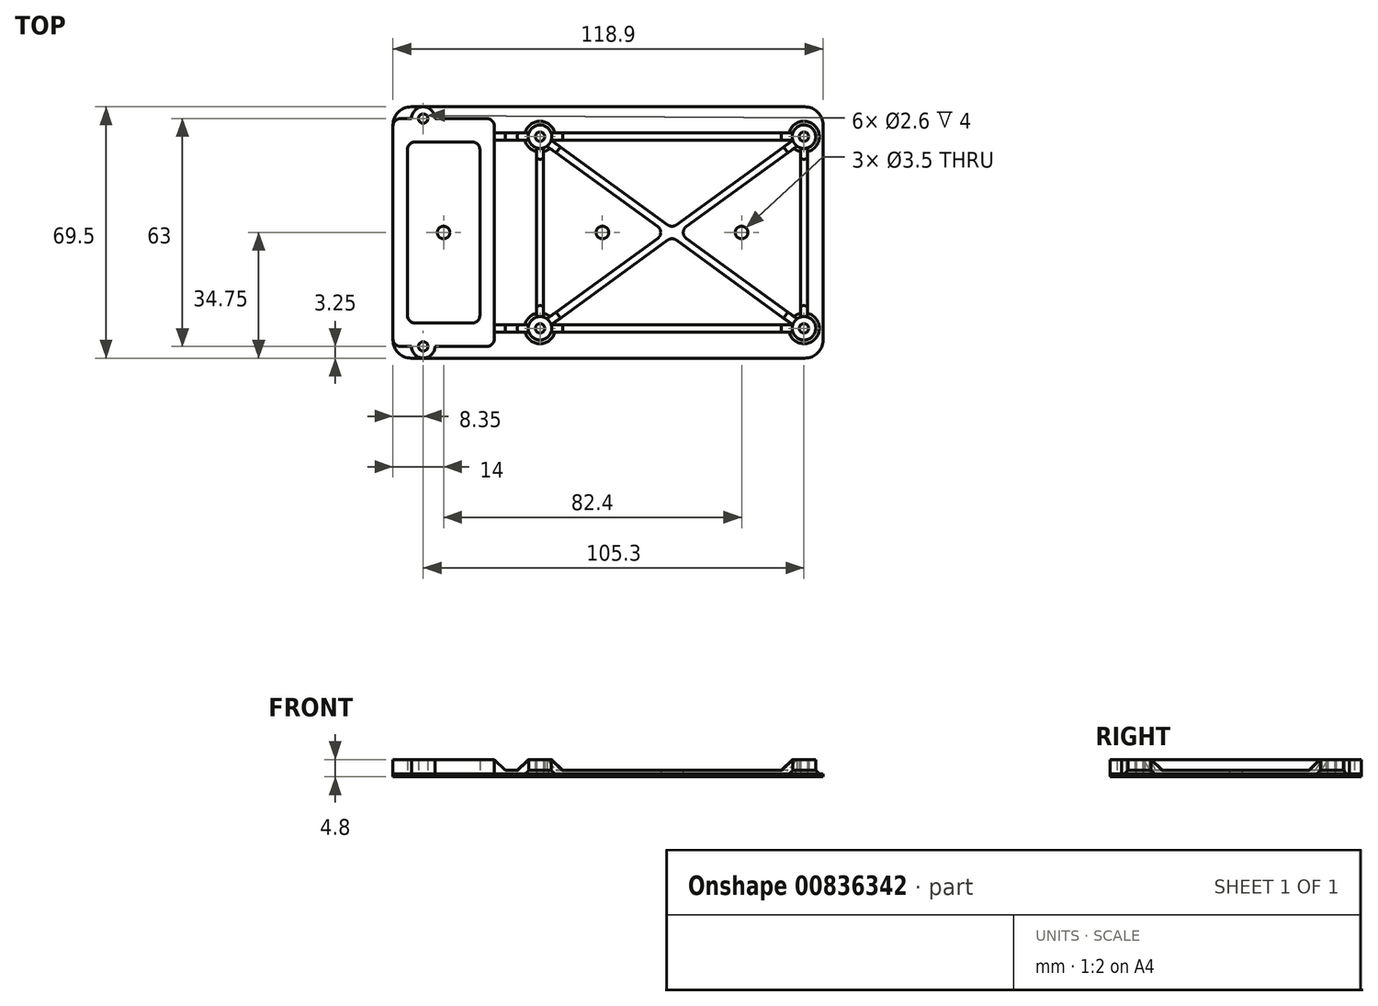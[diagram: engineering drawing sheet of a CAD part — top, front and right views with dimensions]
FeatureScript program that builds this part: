
annotation { "Feature Type Name" : "Feature", "Feature Type Description" : "" }
export const myFeature = defineFeature(function(context is Context, id is Id, definition is map)
    precondition{}
    {
        {
            assignVariable(context, id + "F0", {"name" : "topHoogte", "anyValue" : 4});
        }
        {
            var Q0;
            Q0=qCreatedBy(makeId("Top.planeOp"),FACE);
            var sketch = newSketch(context, id + "F1", { "sketchPlane" : qUnion([Q0])});
            skLineSegment(sketch, "E0.bottom", {"start": v(-19.65, 35) * mm, "end": v(19.65, 35) * mm, "construction": true});
            skLineSegment(sketch, "E0.top", {"start": v(-19.65, -35) * mm, "end": v(19.65, -35) * mm, "construction": true});
            skLineSegment(sketch, "E0.left", {"start": v(-19.65, 35) * mm, "end": v(-19.65, -35) * mm, "construction": true});
            skLineSegment(sketch, "E0.right", {"start": v(19.65, 35) * mm, "end": v(19.65, -35) * mm, "construction": true});
            skPoint(sketch, "E0.middle", {"position": v(0, 0) * mm});
            skLineSegment(sketch, "E1.bottom", {"start": v(118.65, -30) * mm, "end": v(24.65, -30) * mm, "construction": true});
            skLineSegment(sketch, "E1.top", {"start": v(118.65, 30) * mm, "end": v(24.65, 30) * mm, "construction": true});
            skLineSegment(sketch, "E1.left", {"start": v(118.65, -30) * mm, "end": v(118.65, 30) * mm, "construction": true});
            skLineSegment(sketch, "E1.right", {"start": v(24.65, -30) * mm, "end": v(24.65, 30) * mm, "construction": true});
            skPoint(sketch, "E1.middle", {"position": v(71.65, 0) * mm});
            skLineSegment(sketch, "E2", {"start": v(-5.65, 35) * mm, "end": v(-5.65, -35) * mm, "construction": true});
            skPoint(sketch, "E3", {"position": v(-5.65, 31.5) * mm});
            skPoint(sketch, "E4", {"position": v(-5.65, -31.5) * mm});
            skLineSegment(sketch, "E5", {"start": v(24.65, 26.5) * mm, "end": v(118.65, 26.5) * mm, "construction": true});
            skLineSegment(sketch, "E6", {"start": v(24.65, -26.5) * mm, "end": v(118.65, -26.5) * mm, "construction": true});
            skPoint(sketch, "E7", {"position": v(26.65, 26.5) * mm});
            skPoint(sketch, "E8", {"position": v(26.65, -26.5) * mm});
            skPoint(sketch, "E9", {"position": v(99.65, 26.5) * mm});
            skPoint(sketch, "E10", {"position": v(99.65, -26.5) * mm});
            skLineSegment(sketch, "E11", {"start": v(26.65, -26.5) * mm, "end": v(99.65, 26.5) * mm, "construction": true});
            skPoint(sketch, "E12", {"position": v(63.15, 0) * mm});
            skPoint(sketch, "E13", {"position": v(43.9, 0) * mm});
            skLineSegment(sketch, "E14", {"start": v(63.15, 0) * mm, "end": v(63.15, 13.4) * mm, "construction": true});
            skLineSegment(sketch, "E15", {"start": v(63.15, 0) * mm, "end": v(24.65, 0) * mm, "construction": true});
            skPoint(sketch, "E16.MirrorP", {"position": v(82.4, 0) * mm});
            skSolve(sketch);
        }
        {
            var Q0;
            Q0=qCreatedBy(makeId("Top.planeOp"),FACE);
            var sketch = newSketch(context, id + "F2", { "sketchPlane" : qUnion([Q0])});
            skLineSegment(sketch, "E17.bottom", {"start": v(-12, 31.5) * mm, "end": v(12, 31.5) * mm});
            skLineSegment(sketch, "E17.top", {"start": v(-12, -31.5) * mm, "end": v(12, -31.5) * mm});
            skLineSegment(sketch, "E17.left", {"start": v(-14, 29.5) * mm, "end": v(-14, -29.5) * mm});
            skLineSegment(sketch, "E17.right", {"start": v(14, 29.5) * mm, "end": v(14, -29.5) * mm});
            skPoint(sketch, "E17.middle", {"position": v(0, 0) * mm});
            skLineSegment(sketch, "E18.bottom", {"start": v(8, -25) * mm, "end": v(-8, -25) * mm});
            skLineSegment(sketch, "E18.top", {"start": v(8, 25) * mm, "end": v(-8, 25) * mm});
            skLineSegment(sketch, "E18.left", {"start": v(10, -23) * mm, "end": v(10, 23) * mm});
            skLineSegment(sketch, "E18.right", {"start": v(-10, -23) * mm, "end": v(-10, 23) * mm});
            skPoint(sketch, "E19.visualSharp", {"position": v(-10, 25) * mm});
            skArc(sketch, "E19.filletArc", {"start": v(-8, 25) * mm, "mid": v(-9.41, 24.41) * mm, "end": v(-10, 23) * mm});
            skPoint(sketch, "E20.visualSharp", {"position": v(10, 25) * mm});
            skArc(sketch, "E20.filletArc", {"start": v(10, 23) * mm, "mid": v(9.41, 24.41) * mm, "end": v(8, 25) * mm});
            skPoint(sketch, "E21.visualSharp", {"position": v(10, -25) * mm});
            skArc(sketch, "E21.filletArc", {"start": v(8, -25) * mm, "mid": v(9.41, -24.41) * mm, "end": v(10, -23) * mm});
            skPoint(sketch, "E22.visualSharp", {"position": v(-10, -25) * mm});
            skArc(sketch, "E22.filletArc", {"start": v(-10, -23) * mm, "mid": v(-9.41, -24.41) * mm, "end": v(-8, -25) * mm});
            skPoint(sketch, "E23.visualSharp", {"position": v(-14, -31.5) * mm});
            skArc(sketch, "E23.filletArc", {"start": v(-14, -29.5) * mm, "mid": v(-13.41, -30.91) * mm, "end": v(-12, -31.5) * mm});
            skPoint(sketch, "E24.visualSharp", {"position": v(14, -31.5) * mm});
            skArc(sketch, "E24.filletArc", {"start": v(12, -31.5) * mm, "mid": v(13.41, -30.91) * mm, "end": v(14, -29.5) * mm});
            skPoint(sketch, "E25.visualSharp", {"position": v(14, 31.5) * mm});
            skArc(sketch, "E25.filletArc", {"start": v(14, 29.5) * mm, "mid": v(13.41, 30.91) * mm, "end": v(12, 31.5) * mm});
            skPoint(sketch, "E26.visualSharp", {"position": v(-14, 31.5) * mm});
            skArc(sketch, "E26.filletArc", {"start": v(-12, 31.5) * mm, "mid": v(-13.41, 30.91) * mm, "end": v(-14, 29.5) * mm});
            skSolve(sketch);
        }
        {
            var Q0;
            Q0 = qSketchRegion(id + "F2", true);
            extrude(context, id + "F3", {"entities" : qUnion([Q0]), "depth" : (getVariable(context, 'topHoogte')) * mm, "offsetDistance" : 25 * mm});
        }
        {
            var Q0;
            Q0=qCreatedBy(makeId("Top.planeOp"),FACE);
            var sketch = newSketch(context, id + "F4", { "sketchPlane" : qUnion([Q0])});
            skPoint(sketch, "E27", {"position": v(99.65, 26.5) * mm});
            skPoint(sketch, "E28", {"position": v(99.65, -26.5) * mm});
            skLineSegment(sketch, "E29.0", {"start": v(14, 29.5) * mm, "end": v(14, -29.5) * mm, "construction": true});
            skLineSegment(sketch, "E30", {"start": v(99.65, -26.5) * mm, "end": v(14, -26.5) * mm, "construction": true});
            skLineSegment(sketch, "E31", {"start": v(99.65, 26.5) * mm, "end": v(14, 26.5) * mm, "construction": true});
            skLineSegment(sketch, "E32", {"start": v(99.65, 26.5) * mm, "end": v(99.65, -26.5) * mm, "construction": true});
            skArc(sketch, "E33.0.startCap", {"start": v(99.65, 27.5) * mm, "mid": v(100.36, 27.2) * mm, "end": v(100.65, 26.5) * mm});
            skArc(sketch, "E33.0.endCap", {"start": v(14, 25.5) * mm, "mid": v(13, 26.5) * mm, "end": v(14, 27.5) * mm});
            skLineSegment(sketch, "E33.0.right", {"start": v(99.65, 27.5) * mm, "end": v(14, 27.5) * mm});
            skArc(sketch, "E33.1.startCap", {"start": v(99.65, 27.5) * mm, "mid": v(100.36, 27.2) * mm, "end": v(100.65, 26.5) * mm});
            skArc(sketch, "E33.1.endCap", {"start": v(100.65, -26.5) * mm, "mid": v(100.36, -27.2) * mm, "end": v(99.65, -27.5) * mm});
            skLineSegment(sketch, "E33.1.left", {"start": v(100.65, 26.5) * mm, "end": v(100.65, -26.5) * mm});
            skLineSegment(sketch, "E33.1.right", {"start": v(98.65, 24.54) * mm, "end": v(98.65, -24.54) * mm});
            skArc(sketch, "E33.2.startCap", {"start": v(100.65, -26.5) * mm, "mid": v(100.36, -27.2) * mm, "end": v(99.65, -27.5) * mm});
            skArc(sketch, "E33.2.endCap", {"start": v(14, -27.5) * mm, "mid": v(13, -26.5) * mm, "end": v(14, -25.5) * mm});
            skLineSegment(sketch, "E33.2.left", {"start": v(99.65, -27.5) * mm, "end": v(14, -27.5) * mm});
            skPoint(sketch, "E34", {"position": v(26.65, 26.5) * mm});
            skPoint(sketch, "E35", {"position": v(26.65, -26.5) * mm});
            skLineSegment(sketch, "E36", {"start": v(26.65, -26.5) * mm, "end": v(26.65, 26.5) * mm, "construction": true});
            skLineSegment(sketch, "E37", {"start": v(25.65, 25.5) * mm, "end": v(25.65, -25.5) * mm});
            skLineSegment(sketch, "E38", {"start": v(27.65, -24.54) * mm, "end": v(27.65, 24.54) * mm});
            skLineSegment(sketch, "E39.trimOffspring", {"start": v(25.65, -25.5) * mm, "end": v(14, -25.5) * mm});
            skLineSegment(sketch, "E40.trimOffspring", {"start": v(25.65, 25.5) * mm, "end": v(14, 25.5) * mm});
            skLineSegment(sketch, "E41", {"start": v(26.65, 26.5) * mm, "end": v(99.65, -26.5) * mm, "construction": true});
            skLineSegment(sketch, "E42", {"start": v(99.65, 26.5) * mm, "end": v(26.65, -26.5) * mm, "construction": true});
            skLineSegment(sketch, "E43", {"start": v(29.73, 25.5) * mm, "end": v(61.97, 2.09) * mm});
            skLineSegment(sketch, "E44", {"start": v(96.57, -25.5) * mm, "end": v(64.33, -2.09) * mm});
            skLineSegment(sketch, "E45.trimOffspring", {"start": v(96.57, -25.5) * mm, "end": v(29.73, -25.5) * mm});
            skLineSegment(sketch, "E46", {"start": v(27.65, -24.54) * mm, "end": v(59.22, -1.62) * mm});
            skLineSegment(sketch, "E47", {"start": v(98.65, 24.54) * mm, "end": v(67.08, 1.62) * mm});
            skLineSegment(sketch, "E48.trimOffspring", {"start": v(96.57, 25.5) * mm, "end": v(29.73, 25.5) * mm});
            skLineSegment(sketch, "E49.trimOffspring", {"start": v(67.08, -1.62) * mm, "end": v(98.65, -24.54) * mm});
            skLineSegment(sketch, "E50.trimOffspring", {"start": v(64.33, 2.09) * mm, "end": v(96.57, 25.5) * mm});
            skLineSegment(sketch, "E51.trimOffspring", {"start": v(59.22, 1.62) * mm, "end": v(27.65, 24.54) * mm});
            skLineSegment(sketch, "E52.trimOffspring", {"start": v(61.97, -2.09) * mm, "end": v(29.73, -25.5) * mm});
            skPoint(sketch, "E53.trimOffspring.end.orphan", {"position": v(27.65, -25.5) * mm});
            skPoint(sketch, "E54.visualSharp", {"position": v(63.15, -1.24) * mm});
            skArc(sketch, "E54.filletArc", {"start": v(64.33, -2.09) * mm, "mid": v(63.15, -1.7) * mm, "end": v(61.97, -2.09) * mm});
            skPoint(sketch, "E55.visualSharp", {"position": v(64.85, 0) * mm});
            skArc(sketch, "E55.filletArc", {"start": v(67.08, 1.62) * mm, "mid": v(66.26, 0) * mm, "end": v(67.08, -1.62) * mm});
            skPoint(sketch, "E56.visualSharp", {"position": v(61.45, 0) * mm});
            skArc(sketch, "E56.filletArc", {"start": v(59.22, -1.62) * mm, "mid": v(60.04, 0) * mm, "end": v(59.22, 1.62) * mm});
            skPoint(sketch, "E57.visualSharp", {"position": v(63.15, 1.24) * mm});
            skArc(sketch, "E57.filletArc", {"start": v(61.97, 2.09) * mm, "mid": v(63.15, 1.7) * mm, "end": v(64.33, 2.09) * mm});
            skSolve(sketch);
        }
        {
            var Q0;
            Q0 = qSketchRegion(id + "F4", true);
            extrude(context, id + "F5", {"entities" : qUnion([Q0]), "operationType" : NewBodyOperationType.ADD, "depth" : 1 * mm, "offsetDistance" : 25 * mm});
        }
        {
            var Q0;
            Q0=makeQuery(id+"F3.opExtrude","CAP_FACE",FACE,{"disambiguationData":[OSD([sQuery(id+"F2.wireOp",EDGE,"E17.bottom"),sQuery(id+"F2.wireOp",EDGE,"E17.top"),sQuery(id+"F2.wireOp",EDGE,"E17.left"),sQuery(id+"F2.wireOp",EDGE,"E17.right"),sQuery(id+"F2.wireOp",EDGE,"Aoumscto-ISyM-bLo6-r2er-gqb8EqtCcs1s.bottom"),sQuery(id+"F2.wireOp",EDGE,"Aoumscto-ISyM-bLo6-r2er-gqb8EqtCcs1s.top"),sQuery(id+"F2.wireOp",EDGE,"Aoumscto-ISyM-bLo6-r2er-gqb8EqtCcs1s.left"),sQuery(id+"F2.wireOp",EDGE,"Aoumscto-ISyM-bLo6-r2er-gqb8EqtCcs1s.right"),sQuery(id+"F2.wireOp",EDGE,"S9hbntlY-zaf4-CZbE-wMCd-JAsEF4PvGXqu"),sQuery(id+"F2.wireOp",EDGE,"iUlIFxYP-P7sP-15qZ-lrAx-pwGYtXNXY4pD")])],"isStart":true});
            var sketch = newSketch(context, id + "F6", { "sketchPlane" : qUnion([Q0])});
            skCircle(sketch, "E58", {"center": v(-5.65, -31.5) * mm, "radius": 3.25 * mm});
            skCircle(sketch, "E59", {"center": v(-5.65, 31.5) * mm, "radius": 3.25 * mm});
            skCircle(sketch, "E60", {"center": v(99.65, 26.5) * mm, "radius": 3.25 * mm});
            skCircle(sketch, "E61", {"center": v(99.65, -26.5) * mm, "radius": 3.25 * mm});
            skCircle(sketch, "E62", {"center": v(26.65, -26.5) * mm, "radius": 3.25 * mm});
            skCircle(sketch, "E63", {"center": v(26.65, 26.5) * mm, "radius": 3.25 * mm});
            skSolve(sketch);
        }
        {
            var Q0;
            Q0 = qSketchRegion(id + "F6", true);
            extrude(context, id + "F7", {"entities" : qUnion([Q0]), "operationType" : NewBodyOperationType.ADD, "oppositeDirection" : true, "depth" : (getVariable(context, 'topHoogte')) * mm, "offsetDistance" : 25 * mm});
        }
        {
            var Q0;
            Q0=qCreatedBy(makeId("Top.planeOp"),FACE);
            var sketch = newSketch(context, id + "F8", { "sketchPlane" : qUnion([Q0])});
            skLineSegment(sketch, "E64.0", {"start": v(-14, 29.5) * mm, "end": v(-14, -29.5) * mm, "construction": true});
            skArc(sketch, "E65.0", {"start": v(96.56, 27.5) * mm, "mid": v(101.95, 28.8) * mm, "end": v(100.65, 23.4) * mm, "construction": true});
            skLineSegment(sketch, "E66.0", {"start": v(24.65, 26.5) * mm, "end": v(118.65, 26.5) * mm, "construction": true});
            skArc(sketch, "E67.0", {"start": v(100.65, -23.4) * mm, "mid": v(101.95, -28.8) * mm, "end": v(96.56, -27.5) * mm, "construction": true});
            skLineSegment(sketch, "E68.0", {"start": v(24.65, -26.5) * mm, "end": v(118.65, -26.5) * mm, "construction": true});
            skLineSegment(sketch, "E69.bottom", {"start": v(104.9, 34.75) * mm, "end": v(-14, 34.75) * mm});
            skLineSegment(sketch, "E69.top", {"start": v(104.9, -34.75) * mm, "end": v(-14, -34.75) * mm});
            skLineSegment(sketch, "E69.left", {"start": v(102.9, 34.75) * mm, "end": v(102.9, -34.75) * mm, "construction": true});
            skLineSegment(sketch, "E69.right", {"start": v(-14, 34.75) * mm, "end": v(-14, -34.75) * mm});
            skPoint(sketch, "E70", {"position": v(102.9, 26.5) * mm});
            skPoint(sketch, "E71", {"position": v(-5.65, 34.75) * mm});
            skLineSegment(sketch, "E72", {"start": v(104.9, 34.75) * mm, "end": v(104.9, -34.75) * mm});
            skPoint(sketch, "E73.orphan", {"position": v(104.9, -34.75) * mm});
            skSolve(sketch);
        }
        {
            var Q0;
            Q0 = qSketchRegion(id + "F8", true);
            extrude(context, id + "F9", {"entities" : qUnion([Q0]), "operationType" : NewBodyOperationType.ADD, "oppositeDirection" : true, "depth" : 0.8 * mm, "offsetDistance" : 25 * mm});
        }
        {
            var Q0;
            Q0=makeQuery(id+"F9.opExtrude","SWEPT_EDGE",EDGE,{"disambiguationData":[OSD([sQuery(id+"F8.wireOp",EDGE,"E69.top"),sQuery(id+"F8.wireOp",EDGE,"E69.right")])]});
            var Q1;
            Q1=makeQuery(id+"F9.opExtrude","SWEPT_EDGE",EDGE,{"disambiguationData":[OSD([sQuery(id+"F8.wireOp",EDGE,"E69.bottom"),sQuery(id+"F8.wireOp",EDGE,"E69.right")])]});
            var Q2;
            Q2=makeQuery(id+"F9.opExtrude","SWEPT_EDGE",EDGE,{"disambiguationData":[OSD([sQuery(id+"F8.wireOp",EDGE,"E69.bottom"),sQuery(id+"F8.wireOp",EDGE,"E69.left")])]});
            var Q3;
            Q3=makeQuery(id+"F9.opExtrude","SWEPT_EDGE",EDGE,{"disambiguationData":[OSD([sQuery(id+"F8.wireOp",EDGE,"E69.top"),sQuery(id+"F8.wireOp",EDGE,"E69.left")])]});
            fillet(context, id + "F10", {"entities" : qUnion([Q0, Q1, Q2, Q3]), "radius" : 5 * mm, "tangentPropagation" : true, "allowEdgeOverflow" : false});
        }
        {
            var Q0;
            Q0=sQuery(id+"F1.wireOp",VERTEX,"E9");
            var Q1;
            Q1=sQuery(id+"F1.wireOp",VERTEX,"E7");
            var Q2;
            Q2=sQuery(id+"F1.wireOp",VERTEX,"E3");
            var Q3;
            Q3=sQuery(id+"F1.wireOp",VERTEX,"E4");
            var Q4;
            Q4=sQuery(id+"F1.wireOp",VERTEX,"E8");
            var Q5;
            Q5=sQuery(id+"F1.wireOp",VERTEX,"E10");
            var Q6;
            Q6=makeQuery(id+"F3.opExtrude","SWEPT_BODY",BODY,{"disambiguationData":[OSD([sQuery(id+"F2.wireOp",EDGE,"E17.bottom"),sQuery(id+"F2.wireOp",EDGE,"E17.top"),sQuery(id+"F2.wireOp",EDGE,"E17.left"),sQuery(id+"F2.wireOp",EDGE,"Aoumscto-ISyM-bLo6-r2er-gqb8EqtCcs1s.bottom"),sQuery(id+"F2.wireOp",EDGE,"Aoumscto-ISyM-bLo6-r2er-gqb8EqtCcs1s.top"),sQuery(id+"F2.wireOp",EDGE,"Aoumscto-ISyM-bLo6-r2er-gqb8EqtCcs1s.right"),sQuery(id+"F2.wireOp",EDGE,"sPsnzCd1-hEix-0JZU-3coD-6OnEEw0yhwWd"),sQuery(id+"F2.wireOp",EDGE,"XCQeSn6e-DVvC-qXyd-qOtz-2lCuqoaPEOlS")])]});
            hole(context, id + "F11", {"style" : HoleStyle.SIMPLE, "endStyle" : HoleEndStyle.THROUGH, "oppositeDirection" : true, "holeDiameter" : 2.6 * mm, "majorDiameter" : 5 * mm, "isTappedThrough" : true, "tappedDepth" : 12 * mm, "tapClearance" : 3, "locations" : qUnion([Q0, Q1, Q2, Q3, Q4, Q5]), "scope" : qUnion([Q6])});
        }
        {
            var Q0;
            Q0=makeQuery(id+"F7.boolean.opBoolean","INTERSECT",EDGE,{"disambiguationData":[OD(2.0)],"derivedFrom":[makeQuery(id+"F5.opExtrude","CAP_FACE",FACE,{"disambiguationData":[OSD([sQuery(id+"F4.wireOp",EDGE,"E33.0.endCap"),sQuery(id+"F4.wireOp",EDGE,"E33.0.left"),sQuery(id+"F4.wireOp",EDGE,"E33.0.right"),sQuery(id+"F4.wireOp",EDGE,"E33.1.startCap"),sQuery(id+"F4.wireOp",EDGE,"E33.1.left"),sQuery(id+"F4.wireOp",EDGE,"E33.1.right"),sQuery(id+"F4.wireOp",EDGE,"E33.2.startCap"),sQuery(id+"F4.wireOp",EDGE,"E33.2.endCap"),sQuery(id+"F4.wireOp",EDGE,"E33.2.left"),sQuery(id+"F4.wireOp",EDGE,"E33.2.right"),sQuery(id+"F4.wireOp",EDGE,"E37"),sQuery(id+"F4.wireOp",EDGE,"E38"),sQuery(id+"F4.wireOp",EDGE,"E39.trimOffspring"),sQuery(id+"F4.wireOp",EDGE,"E40.trimOffspring")])],"isStart":false}),makeQuery(id+"F7.opExtrude","SWEPT_FACE",FACE,{"disambiguationData":[OSD([sQuery(id+"F6.wireOp",EDGE,"E63")])]})]});
            var Q1;
            Q1=makeQuery(id+"F7.boolean.opBoolean","INTERSECT",EDGE,{"disambiguationData":[OD(1.0)],"derivedFrom":[makeQuery(id+"F5.opExtrude","CAP_FACE",FACE,{"disambiguationData":[OSD([sQuery(id+"F4.wireOp",EDGE,"E33.0.endCap"),sQuery(id+"F4.wireOp",EDGE,"E33.0.left"),sQuery(id+"F4.wireOp",EDGE,"E33.0.right"),sQuery(id+"F4.wireOp",EDGE,"E33.1.startCap"),sQuery(id+"F4.wireOp",EDGE,"E33.1.left"),sQuery(id+"F4.wireOp",EDGE,"E33.1.right"),sQuery(id+"F4.wireOp",EDGE,"E33.2.startCap"),sQuery(id+"F4.wireOp",EDGE,"E33.2.endCap"),sQuery(id+"F4.wireOp",EDGE,"E33.2.left"),sQuery(id+"F4.wireOp",EDGE,"E33.2.right"),sQuery(id+"F4.wireOp",EDGE,"E37"),sQuery(id+"F4.wireOp",EDGE,"E38"),sQuery(id+"F4.wireOp",EDGE,"E39.trimOffspring"),sQuery(id+"F4.wireOp",EDGE,"E40.trimOffspring")])],"isStart":false}),makeQuery(id+"F7.opExtrude","SWEPT_FACE",FACE,{"disambiguationData":[OSD([sQuery(id+"F6.wireOp",EDGE,"E63")])]})]});
            var Q2;
            Q2=makeQuery(id+"F7.boolean.opBoolean","INTERSECT",EDGE,{"disambiguationData":[OD(0.0)],"derivedFrom":[makeQuery(id+"F5.opExtrude","CAP_FACE",FACE,{"disambiguationData":[OSD([sQuery(id+"F4.wireOp",EDGE,"E33.0.endCap"),sQuery(id+"F4.wireOp",EDGE,"E33.0.left"),sQuery(id+"F4.wireOp",EDGE,"E33.0.right"),sQuery(id+"F4.wireOp",EDGE,"E33.1.startCap"),sQuery(id+"F4.wireOp",EDGE,"E33.1.left"),sQuery(id+"F4.wireOp",EDGE,"E33.1.right"),sQuery(id+"F4.wireOp",EDGE,"E33.2.startCap"),sQuery(id+"F4.wireOp",EDGE,"E33.2.endCap"),sQuery(id+"F4.wireOp",EDGE,"E33.2.left"),sQuery(id+"F4.wireOp",EDGE,"E33.2.right"),sQuery(id+"F4.wireOp",EDGE,"E37"),sQuery(id+"F4.wireOp",EDGE,"E38"),sQuery(id+"F4.wireOp",EDGE,"E39.trimOffspring"),sQuery(id+"F4.wireOp",EDGE,"E40.trimOffspring")])],"isStart":false}),makeQuery(id+"F7.opExtrude","SWEPT_FACE",FACE,{"disambiguationData":[OSD([sQuery(id+"F6.wireOp",EDGE,"E63")])]})]});
            var Q3;
            Q3=makeQuery(id+"F7.boolean.opBoolean","INTERSECT",EDGE,{"disambiguationData":[OD(2.0)],"derivedFrom":[makeQuery(id+"F5.opExtrude","CAP_FACE",FACE,{"disambiguationData":[OSD([sQuery(id+"F4.wireOp",EDGE,"E33.0.endCap"),sQuery(id+"F4.wireOp",EDGE,"E33.0.left"),sQuery(id+"F4.wireOp",EDGE,"E33.0.right"),sQuery(id+"F4.wireOp",EDGE,"E33.1.startCap"),sQuery(id+"F4.wireOp",EDGE,"E33.1.left"),sQuery(id+"F4.wireOp",EDGE,"E33.1.right"),sQuery(id+"F4.wireOp",EDGE,"E33.2.startCap"),sQuery(id+"F4.wireOp",EDGE,"E33.2.endCap"),sQuery(id+"F4.wireOp",EDGE,"E33.2.left"),sQuery(id+"F4.wireOp",EDGE,"E33.2.right"),sQuery(id+"F4.wireOp",EDGE,"E37"),sQuery(id+"F4.wireOp",EDGE,"E38"),sQuery(id+"F4.wireOp",EDGE,"E39.trimOffspring"),sQuery(id+"F4.wireOp",EDGE,"E40.trimOffspring")])],"isStart":false}),makeQuery(id+"F7.opExtrude","SWEPT_FACE",FACE,{"disambiguationData":[OSD([sQuery(id+"F6.wireOp",EDGE,"E62")])]})]});
            var Q4;
            Q4=makeQuery(id+"F7.boolean.opBoolean","INTERSECT",EDGE,{"disambiguationData":[OD(0.0)],"derivedFrom":[makeQuery(id+"F5.opExtrude","CAP_FACE",FACE,{"disambiguationData":[OSD([sQuery(id+"F4.wireOp",EDGE,"E33.0.endCap"),sQuery(id+"F4.wireOp",EDGE,"E33.0.left"),sQuery(id+"F4.wireOp",EDGE,"E33.0.right"),sQuery(id+"F4.wireOp",EDGE,"E33.1.startCap"),sQuery(id+"F4.wireOp",EDGE,"E33.1.left"),sQuery(id+"F4.wireOp",EDGE,"E33.1.right"),sQuery(id+"F4.wireOp",EDGE,"E33.2.startCap"),sQuery(id+"F4.wireOp",EDGE,"E33.2.endCap"),sQuery(id+"F4.wireOp",EDGE,"E33.2.left"),sQuery(id+"F4.wireOp",EDGE,"E33.2.right"),sQuery(id+"F4.wireOp",EDGE,"E37"),sQuery(id+"F4.wireOp",EDGE,"E38"),sQuery(id+"F4.wireOp",EDGE,"E39.trimOffspring"),sQuery(id+"F4.wireOp",EDGE,"E40.trimOffspring")])],"isStart":false}),makeQuery(id+"F7.opExtrude","SWEPT_FACE",FACE,{"disambiguationData":[OSD([sQuery(id+"F6.wireOp",EDGE,"E62")])]})]});
            var Q5;
            Q5=makeQuery(id+"F7.boolean.opBoolean","INTERSECT",EDGE,{"disambiguationData":[OD(1.0)],"derivedFrom":[makeQuery(id+"F5.opExtrude","CAP_FACE",FACE,{"disambiguationData":[OSD([sQuery(id+"F4.wireOp",EDGE,"E33.0.endCap"),sQuery(id+"F4.wireOp",EDGE,"E33.0.left"),sQuery(id+"F4.wireOp",EDGE,"E33.0.right"),sQuery(id+"F4.wireOp",EDGE,"E33.1.startCap"),sQuery(id+"F4.wireOp",EDGE,"E33.1.left"),sQuery(id+"F4.wireOp",EDGE,"E33.1.right"),sQuery(id+"F4.wireOp",EDGE,"E33.2.startCap"),sQuery(id+"F4.wireOp",EDGE,"E33.2.endCap"),sQuery(id+"F4.wireOp",EDGE,"E33.2.left"),sQuery(id+"F4.wireOp",EDGE,"E33.2.right"),sQuery(id+"F4.wireOp",EDGE,"E37"),sQuery(id+"F4.wireOp",EDGE,"E38"),sQuery(id+"F4.wireOp",EDGE,"E39.trimOffspring"),sQuery(id+"F4.wireOp",EDGE,"E40.trimOffspring")])],"isStart":false}),makeQuery(id+"F7.opExtrude","SWEPT_FACE",FACE,{"disambiguationData":[OSD([sQuery(id+"F6.wireOp",EDGE,"E62")])]})]});
            var Q6;
            Q6=makeQuery(id+"F7.boolean.opBoolean","INTERSECT",EDGE,{"disambiguationData":[OD(0.0)],"derivedFrom":[makeQuery(id+"F5.opExtrude","CAP_FACE",FACE,{"disambiguationData":[OSD([sQuery(id+"F4.wireOp",EDGE,"E33.0.endCap"),sQuery(id+"F4.wireOp",EDGE,"E33.0.left"),sQuery(id+"F4.wireOp",EDGE,"E33.0.right"),sQuery(id+"F4.wireOp",EDGE,"E33.1.startCap"),sQuery(id+"F4.wireOp",EDGE,"E33.1.left"),sQuery(id+"F4.wireOp",EDGE,"E33.1.right"),sQuery(id+"F4.wireOp",EDGE,"E33.2.startCap"),sQuery(id+"F4.wireOp",EDGE,"E33.2.endCap"),sQuery(id+"F4.wireOp",EDGE,"E33.2.left"),sQuery(id+"F4.wireOp",EDGE,"E33.2.right"),sQuery(id+"F4.wireOp",EDGE,"E37"),sQuery(id+"F4.wireOp",EDGE,"E38"),sQuery(id+"F4.wireOp",EDGE,"E39.trimOffspring"),sQuery(id+"F4.wireOp",EDGE,"E40.trimOffspring")])],"isStart":false}),makeQuery(id+"F7.opExtrude","SWEPT_FACE",FACE,{"disambiguationData":[OSD([sQuery(id+"F6.wireOp",EDGE,"E61")])]})]});
            var Q7;
            Q7=makeQuery(id+"F7.boolean.opBoolean","INTERSECT",EDGE,{"disambiguationData":[OD(0.0)],"derivedFrom":[makeQuery(id+"F5.opExtrude","CAP_FACE",FACE,{"disambiguationData":[OSD([sQuery(id+"F4.wireOp",EDGE,"E33.0.endCap"),sQuery(id+"F4.wireOp",EDGE,"E33.0.left"),sQuery(id+"F4.wireOp",EDGE,"E33.0.right"),sQuery(id+"F4.wireOp",EDGE,"E33.1.startCap"),sQuery(id+"F4.wireOp",EDGE,"E33.1.left"),sQuery(id+"F4.wireOp",EDGE,"E33.1.right"),sQuery(id+"F4.wireOp",EDGE,"E33.2.startCap"),sQuery(id+"F4.wireOp",EDGE,"E33.2.endCap"),sQuery(id+"F4.wireOp",EDGE,"E33.2.left"),sQuery(id+"F4.wireOp",EDGE,"E33.2.right"),sQuery(id+"F4.wireOp",EDGE,"E37"),sQuery(id+"F4.wireOp",EDGE,"E38"),sQuery(id+"F4.wireOp",EDGE,"E39.trimOffspring"),sQuery(id+"F4.wireOp",EDGE,"E40.trimOffspring")])],"isStart":false}),makeQuery(id+"F7.opExtrude","SWEPT_FACE",FACE,{"disambiguationData":[OSD([sQuery(id+"F6.wireOp",EDGE,"E60")])]})]});
            var Q8;
            Q8=makeQuery(id+"F7.boolean.opBoolean","INTERSECT",EDGE,{"disambiguationData":[OD(1.0)],"derivedFrom":[makeQuery(id+"F5.opExtrude","CAP_FACE",FACE,{"disambiguationData":[OSD([sQuery(id+"F4.wireOp",EDGE,"E33.0.endCap"),sQuery(id+"F4.wireOp",EDGE,"E33.0.left"),sQuery(id+"F4.wireOp",EDGE,"E33.0.right"),sQuery(id+"F4.wireOp",EDGE,"E33.1.startCap"),sQuery(id+"F4.wireOp",EDGE,"E33.1.left"),sQuery(id+"F4.wireOp",EDGE,"E33.1.right"),sQuery(id+"F4.wireOp",EDGE,"E33.2.startCap"),sQuery(id+"F4.wireOp",EDGE,"E33.2.endCap"),sQuery(id+"F4.wireOp",EDGE,"E33.2.left"),sQuery(id+"F4.wireOp",EDGE,"E33.2.right"),sQuery(id+"F4.wireOp",EDGE,"E37"),sQuery(id+"F4.wireOp",EDGE,"E38"),sQuery(id+"F4.wireOp",EDGE,"E39.trimOffspring"),sQuery(id+"F4.wireOp",EDGE,"E40.trimOffspring")])],"isStart":false}),makeQuery(id+"F7.opExtrude","SWEPT_FACE",FACE,{"disambiguationData":[OSD([sQuery(id+"F6.wireOp",EDGE,"E60")])]})]});
            var Q9;
            Q9=makeQuery(id+"F5.boolean.opBoolean","INTERSECT",EDGE,{"disambiguationData":[OD(0.0)],"derivedFrom":[makeQuery(id+"F3.opExtrude","SWEPT_FACE",FACE,{"disambiguationData":[OSD([sQuery(id+"F2.wireOp",EDGE,"E17.right")])]}),makeQuery(id+"F5.opExtrude","CAP_FACE",FACE,{"disambiguationData":[OSD([sQuery(id+"F4.wireOp",EDGE,"E33.0.endCap"),sQuery(id+"F4.wireOp",EDGE,"E33.0.left"),sQuery(id+"F4.wireOp",EDGE,"E33.0.right"),sQuery(id+"F4.wireOp",EDGE,"E33.1.startCap"),sQuery(id+"F4.wireOp",EDGE,"E33.1.left"),sQuery(id+"F4.wireOp",EDGE,"E33.1.right"),sQuery(id+"F4.wireOp",EDGE,"E33.2.startCap"),sQuery(id+"F4.wireOp",EDGE,"E33.2.endCap"),sQuery(id+"F4.wireOp",EDGE,"E33.2.left"),sQuery(id+"F4.wireOp",EDGE,"E33.2.right"),sQuery(id+"F4.wireOp",EDGE,"E37"),sQuery(id+"F4.wireOp",EDGE,"E38"),sQuery(id+"F4.wireOp",EDGE,"E39.trimOffspring"),sQuery(id+"F4.wireOp",EDGE,"E40.trimOffspring")])],"isStart":false})]});
            var Q10;
            Q10=makeQuery(id+"F5.boolean.opBoolean","INTERSECT",EDGE,{"disambiguationData":[OD(1.0)],"derivedFrom":[makeQuery(id+"F3.opExtrude","SWEPT_FACE",FACE,{"disambiguationData":[OSD([sQuery(id+"F2.wireOp",EDGE,"E17.right")])]}),makeQuery(id+"F5.opExtrude","CAP_FACE",FACE,{"disambiguationData":[OSD([sQuery(id+"F4.wireOp",EDGE,"E33.0.endCap"),sQuery(id+"F4.wireOp",EDGE,"E33.0.left"),sQuery(id+"F4.wireOp",EDGE,"E33.0.right"),sQuery(id+"F4.wireOp",EDGE,"E33.1.startCap"),sQuery(id+"F4.wireOp",EDGE,"E33.1.left"),sQuery(id+"F4.wireOp",EDGE,"E33.1.right"),sQuery(id+"F4.wireOp",EDGE,"E33.2.startCap"),sQuery(id+"F4.wireOp",EDGE,"E33.2.endCap"),sQuery(id+"F4.wireOp",EDGE,"E33.2.left"),sQuery(id+"F4.wireOp",EDGE,"E33.2.right"),sQuery(id+"F4.wireOp",EDGE,"E37"),sQuery(id+"F4.wireOp",EDGE,"E38"),sQuery(id+"F4.wireOp",EDGE,"E39.trimOffspring"),sQuery(id+"F4.wireOp",EDGE,"E40.trimOffspring")])],"isStart":false})]});
            var Q11;
            Q11=makeQuery(id+"F7.boolean.opBoolean","INTERSECT",EDGE,{"disambiguationData":[OD(3.0)],"derivedFrom":[makeQuery(id+"F5.opExtrude","CAP_FACE",FACE,{"disambiguationData":[OSD([sQuery(id+"F4.wireOp",EDGE,"E33.0.endCap"),sQuery(id+"F4.wireOp",EDGE,"E33.0.left"),sQuery(id+"F4.wireOp",EDGE,"E33.0.right"),sQuery(id+"F4.wireOp",EDGE,"E33.1.startCap"),sQuery(id+"F4.wireOp",EDGE,"E33.1.left"),sQuery(id+"F4.wireOp",EDGE,"E33.1.right"),sQuery(id+"F4.wireOp",EDGE,"E33.2.startCap"),sQuery(id+"F4.wireOp",EDGE,"E33.2.endCap"),sQuery(id+"F4.wireOp",EDGE,"E33.2.left"),sQuery(id+"F4.wireOp",EDGE,"E37"),sQuery(id+"F4.wireOp",EDGE,"E38"),sQuery(id+"F4.wireOp",EDGE,"E39.trimOffspring"),sQuery(id+"F4.wireOp",EDGE,"E40.trimOffspring"),sQuery(id+"F4.wireOp",EDGE,"E43"),sQuery(id+"F4.wireOp",EDGE,"E44"),sQuery(id+"F4.wireOp",EDGE,"E45.trimOffspring")])],"isStart":false}),makeQuery(id+"F7.opExtrude","SWEPT_FACE",FACE,{"disambiguationData":[OSD([sQuery(id+"F6.wireOp",EDGE,"E62")])]})]});
            var Q12;
            Q12=makeQuery(id+"F7.boolean.opBoolean","INTERSECT",EDGE,{"disambiguationData":[OD(2.0)],"derivedFrom":[makeQuery(id+"F5.opExtrude","CAP_FACE",FACE,{"disambiguationData":[OSD([sQuery(id+"F4.wireOp",EDGE,"E33.0.endCap"),sQuery(id+"F4.wireOp",EDGE,"E33.0.left"),sQuery(id+"F4.wireOp",EDGE,"E33.0.right"),sQuery(id+"F4.wireOp",EDGE,"E33.1.startCap"),sQuery(id+"F4.wireOp",EDGE,"E33.1.left"),sQuery(id+"F4.wireOp",EDGE,"E33.1.right"),sQuery(id+"F4.wireOp",EDGE,"E33.2.startCap"),sQuery(id+"F4.wireOp",EDGE,"E33.2.endCap"),sQuery(id+"F4.wireOp",EDGE,"E33.2.left"),sQuery(id+"F4.wireOp",EDGE,"E37"),sQuery(id+"F4.wireOp",EDGE,"E38"),sQuery(id+"F4.wireOp",EDGE,"E39.trimOffspring"),sQuery(id+"F4.wireOp",EDGE,"E40.trimOffspring"),sQuery(id+"F4.wireOp",EDGE,"E43"),sQuery(id+"F4.wireOp",EDGE,"E44"),sQuery(id+"F4.wireOp",EDGE,"E45.trimOffspring")])],"isStart":false}),makeQuery(id+"F7.opExtrude","SWEPT_FACE",FACE,{"disambiguationData":[OSD([sQuery(id+"F6.wireOp",EDGE,"E60")])]})]});
            var Q13;
            Q13=makeQuery(id+"F7.boolean.opBoolean","INTERSECT",EDGE,{"disambiguationData":[OD(3.0)],"derivedFrom":[makeQuery(id+"F5.opExtrude","CAP_FACE",FACE,{"disambiguationData":[OSD([sQuery(id+"F4.wireOp",EDGE,"E33.0.endCap"),sQuery(id+"F4.wireOp",EDGE,"E33.0.right"),sQuery(id+"F4.wireOp",EDGE,"E33.1.startCap"),sQuery(id+"F4.wireOp",EDGE,"E33.1.left"),sQuery(id+"F4.wireOp",EDGE,"E33.1.right"),sQuery(id+"F4.wireOp",EDGE,"E33.2.startCap"),sQuery(id+"F4.wireOp",EDGE,"E33.2.endCap"),sQuery(id+"F4.wireOp",EDGE,"E33.2.left"),sQuery(id+"F4.wireOp",EDGE,"E37"),sQuery(id+"F4.wireOp",EDGE,"E38"),sQuery(id+"F4.wireOp",EDGE,"E39.trimOffspring"),sQuery(id+"F4.wireOp",EDGE,"E40.trimOffspring"),sQuery(id+"F4.wireOp",EDGE,"E43"),sQuery(id+"F4.wireOp",EDGE,"E44"),sQuery(id+"F4.wireOp",EDGE,"E45.trimOffspring"),sQuery(id+"F4.wireOp",EDGE,"E46"),sQuery(id+"F4.wireOp",EDGE,"E47"),sQuery(id+"F4.wireOp",EDGE,"E48.trimOffspring"),sQuery(id+"F4.wireOp",EDGE,"E49.trimOffspring"),sQuery(id+"F4.wireOp",EDGE,"E50.trimOffspring"),sQuery(id+"F4.wireOp",EDGE,"E51.trimOffspring"),sQuery(id+"F4.wireOp",EDGE,"E52.trimOffspring"),sQuery(id+"F4.wireOp",EDGE,"E54.filletArc"),sQuery(id+"F4.wireOp",EDGE,"E55.filletArc"),sQuery(id+"F4.wireOp",EDGE,"E56.filletArc"),sQuery(id+"F4.wireOp",EDGE,"E57.filletArc")])],"isStart":false}),makeQuery(id+"F7.opExtrude","SWEPT_FACE",FACE,{"disambiguationData":[OSD([sQuery(id+"F6.wireOp",EDGE,"E63")])]})]});
            chamfer(context, id + "F12", {"entities" : qUnion([Q0, Q1, Q2, Q3, Q4, Q5, Q6, Q7, Q8, Q9, Q10, Q11, Q12, Q13]), "width" : 3 * mm, "tangentPropagation" : true});
        }
        {
            var Q0;
            {var subQ0=sQuery(id+"F6.wireOp",EDGE,"E62");var subQ2=sQuery(id+"F4.wireOp",EDGE,"E37");Q0=makeQuery(id+"F7.boolean.opBoolean","SPLIT",EDGE,{"disambiguationData":[TD([makeQuery(id+"F5.opExtrude","SWEPT_FACE",FACE,{"disambiguationData":[OSD([subQ2])]})])],"derivedFrom":makeQuery(id+"F7.opExtrude","CAP_EDGE",EDGE,{"disambiguationData":[OSD([subQ0])],"isStart":true})});}
            var Q1;
            {var subQ0=sQuery(id+"F6.wireOp",EDGE,"E62");var subQ2=sQuery(id+"F4.wireOp",EDGE,"E38");Q1=makeQuery(id+"F7.boolean.opBoolean","SPLIT",EDGE,{"disambiguationData":[TD([makeQuery(id+"F5.opExtrude","SWEPT_FACE",FACE,{"disambiguationData":[OSD([subQ2])]})])],"derivedFrom":makeQuery(id+"F7.opExtrude","CAP_EDGE",EDGE,{"disambiguationData":[OSD([subQ0])],"isStart":true})});}
            var Q2;
            {var subQ0=sQuery(id+"F6.wireOp",EDGE,"E62");var subQ1=sQuery(id+"F4.wireOp",EDGE,"E33.0.right");Q2=makeQuery(id+"F7.boolean.opBoolean","SPLIT",EDGE,{"disambiguationData":[TD([makeQuery(id+"F5.opExtrude","SWEPT_FACE",FACE,{"disambiguationData":[OSD([subQ1])]})])],"derivedFrom":makeQuery(id+"F7.opExtrude","CAP_EDGE",EDGE,{"disambiguationData":[OSD([subQ0])],"isStart":true})});}
            var Q3;
            {var subQ0=sQuery(id+"F4.wireOp",EDGE,"E33.2.left");var subQ1=sQuery(id+"F6.wireOp",EDGE,"E63");Q3=makeQuery(id+"F7.boolean.opBoolean","SPLIT",EDGE,{"disambiguationData":[TD([makeQuery(id+"F5.opExtrude","SWEPT_FACE",FACE,{"disambiguationData":[OSD([subQ0])]})])],"derivedFrom":makeQuery(id+"F7.opExtrude","CAP_EDGE",EDGE,{"disambiguationData":[OSD([subQ1])],"isStart":true})});}
            var Q4;
            {var subQ0=sQuery(id+"F6.wireOp",EDGE,"E63");var subQ1=sQuery(id+"F4.wireOp",EDGE,"E37");Q4=makeQuery(id+"F7.boolean.opBoolean","SPLIT",EDGE,{"disambiguationData":[TD([makeQuery(id+"F5.opExtrude","SWEPT_FACE",FACE,{"disambiguationData":[OSD([subQ1])]})])],"derivedFrom":makeQuery(id+"F7.opExtrude","CAP_EDGE",EDGE,{"disambiguationData":[OSD([subQ0])],"isStart":true})});}
            var Q5;
            {var subQ0=sQuery(id+"F6.wireOp",EDGE,"E63");var subQ2=sQuery(id+"F4.wireOp",EDGE,"E38");Q5=makeQuery(id+"F7.boolean.opBoolean","SPLIT",EDGE,{"disambiguationData":[TD([makeQuery(id+"F5.opExtrude","SWEPT_FACE",FACE,{"disambiguationData":[OSD([subQ2])]})])],"derivedFrom":makeQuery(id+"F7.opExtrude","CAP_EDGE",EDGE,{"disambiguationData":[OSD([subQ0])],"isStart":true})});}
            var Q6;
            {var subQ0=sQuery(id+"F4.wireOp",EDGE,"E33.2.left");var subQ1=makeQuery(id+"F5.opExtrude","SWEPT_FACE",FACE,{"disambiguationData":[OSD([subQ0])]});var subQ2=sQuery(id+"F6.wireOp",EDGE,"E60");var subQ5=sQuery(id+"F4.wireOp",EDGE,"E33.1.left");Q6=makeQuery(id+"F9.boolean.opBoolean","SPLIT",EDGE,{"disambiguationData":[TD([subQ1])],"derivedFrom":makeQuery(id+"F7.boolean.opBoolean","SPLIT",EDGE,{"disambiguationData":[TD([makeQuery(id+"F5.opExtrude","SWEPT_FACE",FACE,{"disambiguationData":[OSD([subQ5])]})])],"derivedFrom":makeQuery(id+"F7.opExtrude","CAP_EDGE",EDGE,{"disambiguationData":[OSD([subQ2])],"isStart":true})})});}
            var Q7;
            {var subQ0=sQuery(id+"F6.wireOp",EDGE,"E60");var subQ2=sQuery(id+"F4.wireOp",EDGE,"E33.1.right");Q7=makeQuery(id+"F7.boolean.opBoolean","SPLIT",EDGE,{"disambiguationData":[TD([makeQuery(id+"F5.opExtrude","SWEPT_FACE",FACE,{"disambiguationData":[OSD([subQ2])]})])],"derivedFrom":makeQuery(id+"F7.opExtrude","CAP_EDGE",EDGE,{"disambiguationData":[OSD([subQ0])],"isStart":true})});}
            var Q8;
            {var subQ0=sQuery(id+"F4.wireOp",EDGE,"E33.0.right");var subQ1=makeQuery(id+"F5.opExtrude","SWEPT_FACE",FACE,{"disambiguationData":[OSD([subQ0])]});var subQ2=sQuery(id+"F6.wireOp",EDGE,"E61");Q8=makeQuery(id+"F9.boolean.opBoolean","SPLIT",EDGE,{"disambiguationData":[TD([subQ1])],"derivedFrom":makeQuery(id+"F7.boolean.opBoolean","SPLIT",EDGE,{"disambiguationData":[TD([subQ1])],"derivedFrom":makeQuery(id+"F7.opExtrude","CAP_EDGE",EDGE,{"disambiguationData":[OSD([subQ2])],"isStart":true})})});}
            var Q9;
            {var subQ0=sQuery(id+"F6.wireOp",EDGE,"E61");var subQ2=sQuery(id+"F4.wireOp",EDGE,"E33.1.right");Q9=makeQuery(id+"F7.boolean.opBoolean","SPLIT",EDGE,{"disambiguationData":[TD([makeQuery(id+"F5.opExtrude","SWEPT_FACE",FACE,{"disambiguationData":[OSD([subQ2])]})])],"derivedFrom":makeQuery(id+"F7.opExtrude","CAP_EDGE",EDGE,{"disambiguationData":[OSD([subQ0])],"isStart":true})});}
            chamfer(context, id + "F13", {"entities" : qUnion([Q0, Q1, Q2, Q3, Q4, Q5, Q6, Q7, Q8, Q9]), "width" : 1 * mm, "tangentPropagation" : true});
        }
        {
            var Q0;
            Q0=sQuery(id+"F1.wireOp",VERTEX,"E0.middle");
            var Q1;
            Q1=sQuery(id+"F1.wireOp",VERTEX,"E13");
            var Q2;
            Q2=sQuery(id+"F1.wireOp",VERTEX,"E16.MirrorP");
            var Q3;
            Q3=makeQuery(id+"F3.opExtrude","SWEPT_BODY",BODY,{"disambiguationData":[OSD([sQuery(id+"F2.wireOp",EDGE,"E17.bottom"),sQuery(id+"F2.wireOp",EDGE,"E17.top"),sQuery(id+"F2.wireOp",EDGE,"E17.left"),sQuery(id+"F2.wireOp",EDGE,"E17.right"),sQuery(id+"F2.wireOp",EDGE,"E18.bottom"),sQuery(id+"F2.wireOp",EDGE,"E18.top"),sQuery(id+"F2.wireOp",EDGE,"E18.left"),sQuery(id+"F2.wireOp",EDGE,"E18.right"),sQuery(id+"F2.wireOp",EDGE,"E19.filletArc"),sQuery(id+"F2.wireOp",EDGE,"E20.filletArc"),sQuery(id+"F2.wireOp",EDGE,"E21.filletArc"),sQuery(id+"F2.wireOp",EDGE,"E22.filletArc"),sQuery(id+"F2.wireOp",EDGE,"E23.filletArc"),sQuery(id+"F2.wireOp",EDGE,"E24.filletArc"),sQuery(id+"F2.wireOp",EDGE,"E25.filletArc"),sQuery(id+"F2.wireOp",EDGE,"E26.filletArc")])]});
            hole(context, id + "F14", {"style" : HoleStyle.SIMPLE, "endStyle" : HoleEndStyle.THROUGH, "holeDiameter" : 3.5 * mm, "majorDiameter" : 5 * mm, "isTappedThrough" : true, "tappedDepth" : 12 * mm, "tapClearance" : 3, "locations" : qUnion([Q0, Q1, Q2]), "scope" : qUnion([Q3])});
        }
    });
